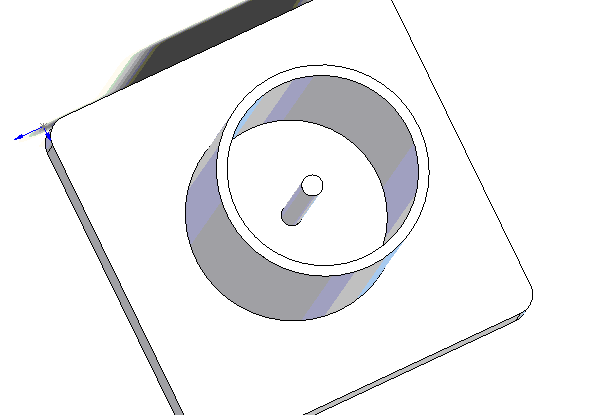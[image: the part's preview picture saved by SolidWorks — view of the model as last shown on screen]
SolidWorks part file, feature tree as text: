
SOLIDWORKS PART (.sldprt)
format: sldprt  version: not decoded by parser v0  size: 150,016 bytes
history: native  units: mm
features: sketch x5, extrude x4, material x1, cut_extrude x1 (+13 scaffold rows collapsed)
feature tree (24):
  scaffold x13  (default folders/planes/origin — collapsed)
  material  "Material <not specified>"
  sketch  "Sketch1"  dims[D3=1.0mm D1=17.45mm D2=17.45mm]
  extrude  "Extrude1"  Depth=2.36mm
  sketch  "Sketch2"  dims[D1=10.0mm D2=8.725mm D3=8.725mm]
  extrude  "Extrude2"  Depth=13.52mm
  sketch  "Sketch3"  dims[D1=9.0mm]
  cut_extrude  "Cut-Extrude1"  Depth=13.52mm
  sketch  "Sketch4"  dims[D1=1.0mm D4=1.0mm D5=1.0mm D6=1.0mm D7=1.0mm D2=8.725mm D3=8.725mm D8=6.35mm D9=6.35mm D10=6.35mm D11=6.35mm D12=6.35mm]
  extrude  "Extrude3"  Depth=6.5mm
  sketch  "Sketch5"  dims[D1=1.0mm]
  extrude  "Extrude4"  Depth=9mm
decode coverage: 10 of 10 modeling features carry decoded parameters
note: suppression state not decoded; provenance and decode notes live in map.json
